# Revit family: Hager-Univers-IP44-D161-3rows-Cl.II-FWB_encl_empty-AT-de
name_source: partatom
category: Equipement électrique
units: mm (PartAtom-declared; Revit-internal decimal feet)

## family parameters
Configuration du panneau = Deux colonnes, circuits au sein
Cote de connecteur circulaire = Utiliser le diamètre
Couper avec des vides une fois chargée = Non
Hôte = Face
Partagée = Non
Point de calcul de pièce = Non
Type d'élément = Tableau de raccordement

## types (1)
- Aufputz IP44 B300 H500 T161  - FWB31D
    Commentaires du type = Univers
    EF000003 - Montageart = EV000384 - Aufputz
    EF000007 - Farbe = EV000202 - weiß
    EF000008 - Breite = 300 mm  [stored 0.984252 ft]
    EF000040 - Höhe = 500 mm  [stored 1.64042 ft]
    EF000049 - Tiefe = 161 mm  [stored 0.528215 ft]
    EF000116 - RAL-Nummer = 9010
    EF000118 - Mit Montageplatte = Non
    EF000218 - Einbautiefe = 0 mm  [stored 0 ft]
    EF000266 - Anzahl der Reihen = 0
    EF000339 - Art der Abdeckung = EV004216 - Tür
    EF000437 - Anzahl der Leitungseinführungen = 4
    EF001088 - Anbaumöglichkeit = Oui
    EF001131 - Innentiefe = 156 mm
    EF001596 - Werkstoff des Gehäuses = EV000179 - Stahl
    EF001613 - Funktionserhalt = EV000494 - ohne
    EF002950 - Breite in Teilungseinheiten = 12
    EF003532 - Geeignet für Außengebrauch = Non
    EF004293 - Schlagfestigkeit = EV006815 - IK09
    EF004427 - Anzahl der Module = 36
    EF004464 - Art der Tür = EV002646 - Einzel
    EF005474 - Schutzart (IP) = EV006418 - IP44
    EF006244 - Transparenter Deckel/Tür = Non
    EF006306 - Mit Schloss = Non
    EF007800 - Geeignet für Blitzschutz = Non
    EF008873 - Nennstrom (In) = 125 A
    EF009170 - Materialstärke Gehäuse = 2 mm  [stored 0.00656168 ft]
    EF009171 - Materialstärke Tür/Deckel = 2 mm  [stored 0.00656168 ft]
    EF009212 - Ausführung Deckel = EV000116 - geschlossen
    EF009554 - Anzahl der Öffnungen für Flanschplatten = 2
    EF015940 - Deckel mit Überdruckentlastung = Non
    Elévation par défaut = 0 mm  [stored 0 ft]
    Fabricant = Hager
    HG000002 - Mit tür = Oui
    HG000003 - Bereich = Univers
    HG000004 - Herstellerreferenz = FWB31D
    HG000006 - Unterputz = Non
    HG000009 - Doppelflügeligen Tür = Non
    HG000010 - Asymmetrische Türen = Non
    HG000023 - Gehäuse mit doppeltem Querschnitt = Non
    HG000024 - Höhe des unteren Teils = 800 mm  [stored 2.62467 ft]
    HG000026 - Stehend auf dem Boden = Non
    HG000027 - Sockelhöhe = 0 mm  [stored 0 ft]

note: [stored X ft] marks values corroborated as IEEE doubles in the binary element streams (Revit-internal decimal feet)

## geometry (parser evidence)
native form markers: Sweep x9
no freeform markers — native parametric forms only
